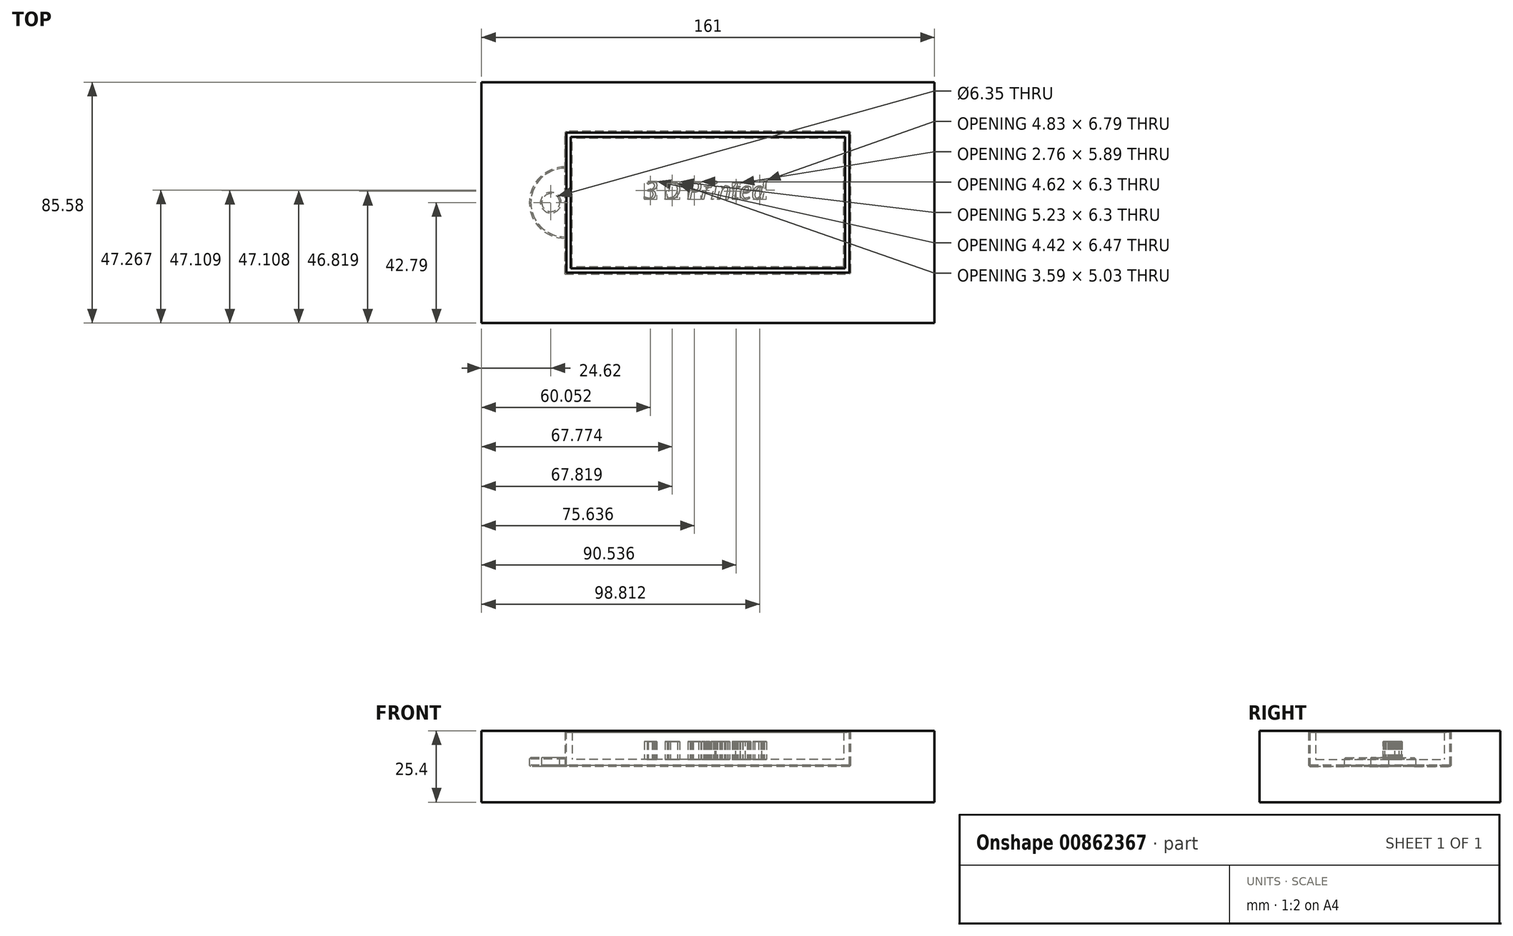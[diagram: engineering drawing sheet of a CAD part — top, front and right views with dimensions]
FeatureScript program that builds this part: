
annotation { "Feature Type Name" : "Feature", "Feature Type Description" : "" }
export const myFeature = defineFeature(function(context is Context, id is Id, definition is map)
    precondition{}
    {
        {
            var Q0;
            Q0=qCreatedBy(makeId("Top.planeOp"),FACE);
            var sketch = newSketch(context, id + "F0", { "sketchPlane" : qUnion([Q0])});
            skLineSegment(sketch, "E0.bottom", {"start": v(50.8, -25.4) * mm, "end": v(-50.8, -25.4) * mm});
            skLineSegment(sketch, "E0.top", {"start": v(50.8, 25.4) * mm, "end": v(-50.8, 25.4) * mm});
            skLineSegment(sketch, "E0.left", {"start": v(50.8, -25.4) * mm, "end": v(50.8, 25.4) * mm});
            skLineSegment(sketch, "E0.right", {"start": v(-50.8, -25.4) * mm, "end": v(-50.8, 25.4) * mm});
            skPoint(sketch, "E0.middle", {"position": v(0, 0) * mm});
            skSolve(sketch);
        }
        {
            var Q0;
            Q0=makeQuery(id+"F0.imprint","IMPRINT",FACE,{"disambiguationData":[TD([[makeQuery(id+"F0.imprint","IMPRINT",EDGE,{"derivedFrom":sQuery(id+"F0.wireOp",EDGE,"E0.bottom")}),-1.0]])]});
            extrude(context, id + "F1", {"entities" : qUnion([Q0]), "depth" : 12.7 * mm, "offsetDistance" : 25.4 * mm});
        }
        {
            var Q0;
            Q0=makeQuery(id+"F1.opExtrude","CAP_FACE",FACE,{"disambiguationData":[OSD([sQuery(id+"F0.wireOp",EDGE,"E0.bottom"),sQuery(id+"F0.wireOp",EDGE,"E0.top"),sQuery(id+"F0.wireOp",EDGE,"E0.left"),sQuery(id+"F0.wireOp",EDGE,"E0.right")])],"isStart":false});
            shell(context, id + "F2", {"entities" : qUnion([Q0]), "thickness" : 2.54 * mm});
        }
        {
            var Q0;
            Q0=makeQuery(id+"F2.opShell","OFFSET_FACE",FACE,{"disambiguationData":[OSD([sQuery(id+"F0.wireOp",EDGE,"E0.bottom"),sQuery(id+"F0.wireOp",EDGE,"E0.top"),sQuery(id+"F0.wireOp",EDGE,"E0.left"),sQuery(id+"F0.wireOp",EDGE,"E0.right")])]});
            var sketch = newSketch(context, id + "F3", { "sketchPlane" : qUnion([Q0])});
            skText(sketch, "E1", { "text": "3 D Printed", "fontName": "OpenSans-Italic.ttf"});
            const initialGuessF3  = {"E1": [-0.02286, 0.00117, 1, 0, 0.00635]};
            skSetInitialGuess(sketch, initialGuessF3);
            skSolve(sketch);
        }
        {
            var Q0;
            Q0 = qSketchRegion(id + "F3", true);
            extrude(context, id + "F4", {"entities" : qUnion([Q0]), "operationType" : NewBodyOperationType.ADD, "depth" : 6.35 * mm, "offsetDistance" : 25.4 * mm});
        }
        {
            var Q0;
            Q0=makeQuery(id+"F1.opExtrude","CAP_FACE",FACE,{"disambiguationData":[OSD([sQuery(id+"F0.wireOp",EDGE,"E0.bottom"),sQuery(id+"F0.wireOp",EDGE,"E0.top"),sQuery(id+"F0.wireOp",EDGE,"E0.left"),sQuery(id+"F0.wireOp",EDGE,"E0.right")])],"isStart":true});
            var sketch = newSketch(context, id + "F5", { "sketchPlane" : qUnion([Q0])});
            skCircle(sketch, "E2", {"center": v(-50.8, 0) * mm, "radius": 12.7 * mm});
            skSolve(sketch);
        }
        {
            var Q0;
            {var subQ0=sQuery(id+"F5.wireOp",EDGE,"E2");var subQ1=makeQuery(id+"F1.opExtrude","CAP_EDGE",EDGE,{"disambiguationData":[OSD([sQuery(id+"F0.wireOp",EDGE,"E0.right")])],"isStart":true});var subQ2=makeQuery(id+"F5.imprint","INTERSECT",VERTEX,{"disambiguationData":[OD(0.0)],"derivedFrom":[subQ1,subQ0]});Q0=makeQuery(id+"F5.imprint","IMPRINT",FACE,{"disambiguationData":[TD([[makeQuery(id+"F5.imprint","IMPRINT",EDGE,{"disambiguationData":[TD([[subQ2,-1.0]])],"derivedFrom":subQ0}),1.0]])]});}
            extrude(context, id + "F6", {"entities" : qUnion([Q0]), "operationType" : NewBodyOperationType.ADD, "oppositeDirection" : true, "depth" : 3.17 * mm, "offsetDistance" : 25.4 * mm});
        }
        {
            var Q0;
            Q0=makeQuery(id+"F6.opExtrude","CAP_FACE",FACE,{"disambiguationData":[OSD([sQuery(id+"F0.wireOp",EDGE,"E0.right"),sQuery(id+"F5.wireOp",EDGE,"E2")])],"isStart":false});
            var sketch = newSketch(context, id + "F7", { "sketchPlane" : qUnion([Q0])});
            skCircle(sketch, "E3", {"center": v(-55.88, 0) * mm, "radius": 3.18 * mm});
            skSolve(sketch);
        }
        {
            var Q0;
            Q0=makeQuery(id+"F7.imprint","IMPRINT",FACE,{"disambiguationData":[TD([[makeQuery(id+"F7.imprint","IMPRINT",EDGE,{"derivedFrom":sQuery(id+"F7.wireOp",EDGE,"E3")}),1.0]])]});
            extrude(context, id + "F8", {"entities" : qUnion([Q0]), "operationType" : NewBodyOperationType.REMOVE, "oppositeDirection" : true, "depth" : 25.4 * mm, "offsetDistance" : 25.4 * mm});
        }
        {
            var Q0;
            {var subQ0=sQuery(id+"F0.wireOp",EDGE,"E0.right");Q0=makeQuery(id+"F6.boolean.opBoolean","MERGE",FACE,{"derivedFrom":[makeQuery(id+"F1.opExtrude","CAP_FACE",FACE,{"disambiguationData":[OSD([sQuery(id+"F0.wireOp",EDGE,"E0.bottom"),sQuery(id+"F0.wireOp",EDGE,"E0.top"),sQuery(id+"F0.wireOp",EDGE,"E0.left"),subQ0])],"isStart":true}),makeQuery(id+"F6.opExtrude","CAP_FACE",FACE,{"disambiguationData":[OSD([subQ0,sQuery(id+"F5.wireOp",EDGE,"E2")])],"isStart":true})]});}
            var Q1;
            Q1=makeQuery(id+"F1.opExtrude","CAP_FACE",FACE,{"disambiguationData":[OSD([sQuery(id+"F0.wireOp",EDGE,"E0.bottom"),sQuery(id+"F0.wireOp",EDGE,"E0.top"),sQuery(id+"F0.wireOp",EDGE,"E0.left"),sQuery(id+"F0.wireOp",EDGE,"E0.right")])],"isStart":false});
            chamfer(context, id + "F9", {"entities" : qUnion([Q0, Q1]), "width" : 0.5 * mm, "tangentPropagation" : true});
        }
        {
            var Q0;
            Q0=makeQuery(id+"F6.opExtrude","CAP_EDGE",EDGE,{"disambiguationData":[OSD([sQuery(id+"F5.wireOp",EDGE,"E2")])],"isStart":false});
            var Q1;
            Q1=makeQuery(id+"F8.boolean.opBoolean","COPY",EDGE,{"derivedFrom":makeQuery(id+"F8.opExtrude","CAP_EDGE",EDGE,{"disambiguationData":[OSD([sQuery(id+"F7.wireOp",EDGE,"E3")])],"isStart":true})});
            chamfer(context, id + "F10", {"entities" : qUnion([Q0, Q1]), "width" : 0.5 * mm, "tangentPropagation" : true});
        }
        {
            var Q0;
            Q0=makeQuery(id+"F1.opExtrude","SWEPT_EDGE",EDGE,{"disambiguationData":[OSD([sQuery(id+"F0.wireOp",EDGE,"E0.top"),sQuery(id+"F0.wireOp",EDGE,"E0.right")])]});
            var Q1;
            Q1=makeQuery(id+"F1.opExtrude","SWEPT_EDGE",EDGE,{"disambiguationData":[OSD([sQuery(id+"F0.wireOp",EDGE,"E0.bottom"),sQuery(id+"F0.wireOp",EDGE,"E0.left")])]});
            var Q2;
            Q2=makeQuery(id+"F1.opExtrude","SWEPT_EDGE",EDGE,{"disambiguationData":[OSD([sQuery(id+"F0.wireOp",EDGE,"E0.top"),sQuery(id+"F0.wireOp",EDGE,"E0.left")])]});
            chamfer(context, id + "F11", {"entities" : qUnion([Q0, Q1, Q2]), "width" : 0.5 * mm, "tangentPropagation" : true});
        }
        {
            var Q0;
            {var subQ0=sQuery(id+"F0.wireOp",EDGE,"E0.right");Q0=makeQuery(id+"F6.boolean.opBoolean","MERGE",FACE,{"derivedFrom":[makeQuery(id+"F1.opExtrude","CAP_FACE",FACE,{"disambiguationData":[OSD([sQuery(id+"F0.wireOp",EDGE,"E0.bottom"),sQuery(id+"F0.wireOp",EDGE,"E0.top"),sQuery(id+"F0.wireOp",EDGE,"E0.left"),subQ0])],"isStart":true}),makeQuery(id+"F6.opExtrude","CAP_FACE",FACE,{"disambiguationData":[OSD([subQ0,sQuery(id+"F5.wireOp",EDGE,"E2")])],"isStart":true})]});}
            var sketch = newSketch(context, id + "F12", { "sketchPlane" : qUnion([Q0])});
            skLineSegment(sketch, "E4.bottom", {"start": v(-80.5, -42.79) * mm, "end": v(80.5, -42.79) * mm});
            skLineSegment(sketch, "E4.top", {"start": v(-80.5, 42.79) * mm, "end": v(80.5, 42.79) * mm});
            skLineSegment(sketch, "E4.left", {"start": v(-80.5, -42.79) * mm, "end": v(-80.5, 42.79) * mm});
            skLineSegment(sketch, "E4.right", {"start": v(80.5, -42.79) * mm, "end": v(80.5, 42.79) * mm});
            skPoint(sketch, "E4.middle", {"position": v(0, 0) * mm});
            skSolve(sketch);
        }
        {
            var Q0;
            Q0 = qSketchRegion(id + "F12", true);
            extrude(context, id + "F13", {"entities" : qUnion([Q0]), "endBound" : BoundingType.SYMMETRIC, "depth" : 25.4 * mm, "offsetDistance" : 25.4 * mm});
        }
        {
            var Q0;
            Q0=makeQuery(id+"F1.opExtrude","SWEPT_BODY",BODY,{"disambiguationData":[OSD([sQuery(id+"F0.wireOp",EDGE,"E0.bottom"),sQuery(id+"F0.wireOp",EDGE,"E0.top"),sQuery(id+"F0.wireOp",EDGE,"E0.left"),sQuery(id+"F0.wireOp",EDGE,"E0.right")])]});
            var Q1;
            Q1=makeQuery(id+"F13.opExtrude","SWEPT_BODY",BODY,{"disambiguationData":[OSD([sQuery(id+"F12.wireOp",EDGE,"E4.bottom"),sQuery(id+"F12.wireOp",EDGE,"E4.top"),sQuery(id+"F12.wireOp",EDGE,"E4.left"),sQuery(id+"F12.wireOp",EDGE,"E4.right")])]});
            booleanBodies(context, id + "F14", {"operationType" : BooleanOperationType.SUBTRACTION, "tools" : qUnion([Q0]), "targets" : qUnion([Q1]), "keepTools" : true});
        }
    });
